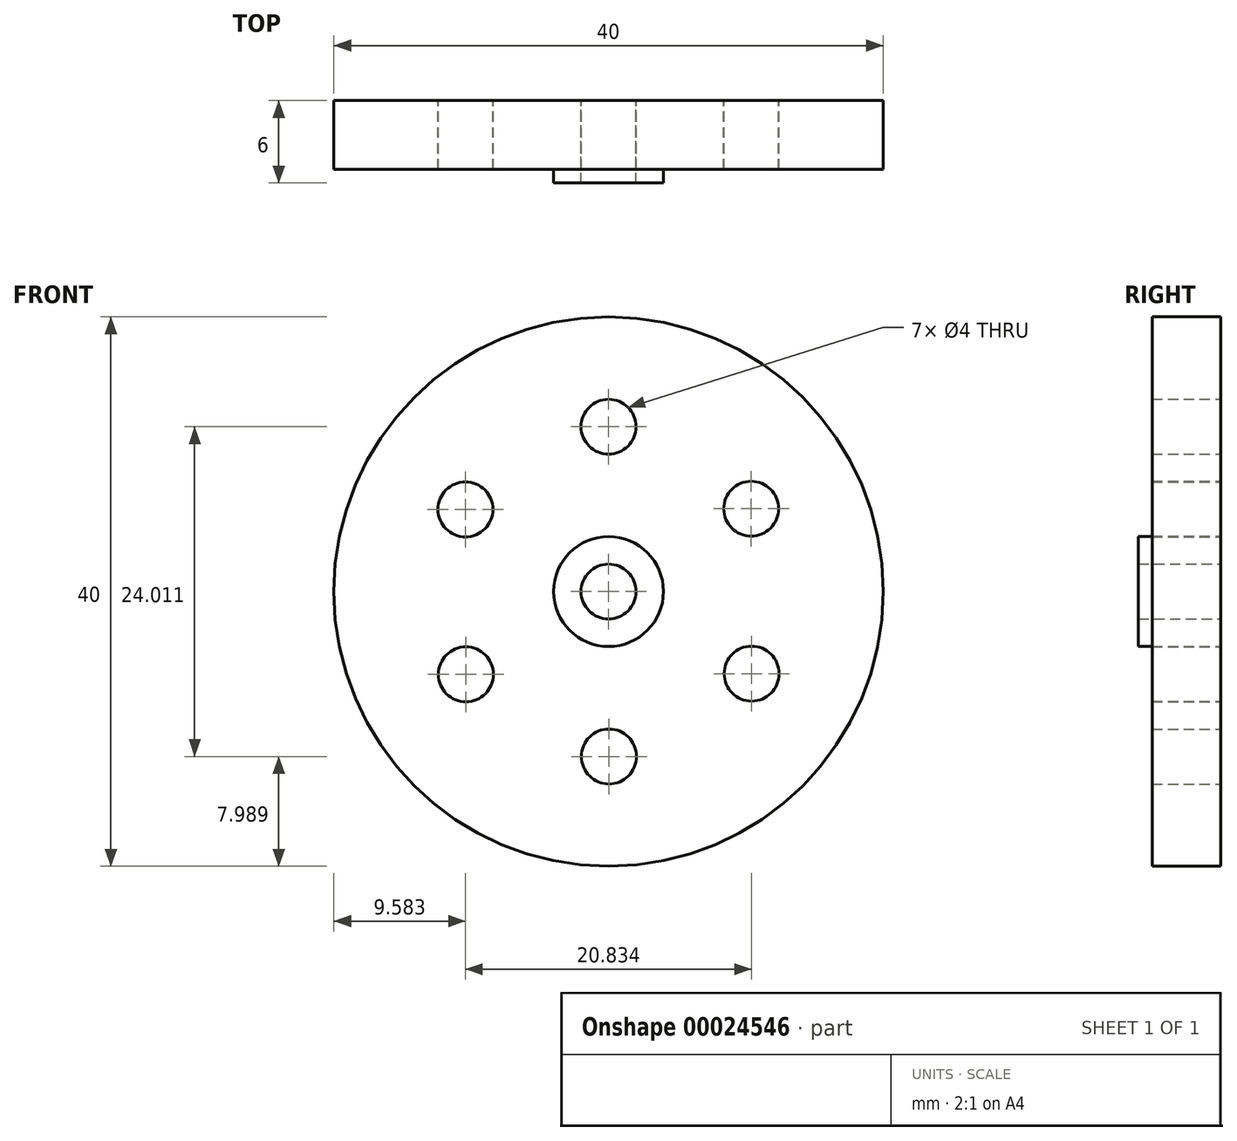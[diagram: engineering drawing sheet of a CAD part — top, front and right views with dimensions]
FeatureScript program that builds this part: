
annotation { "Feature Type Name" : "Feature", "Feature Type Description" : "" }
export const myFeature = defineFeature(function(context is Context, id is Id, definition is map)
    precondition{}
    {
        {
            var Q0;
            Q0=qCreatedBy(makeId("Front.planeOp"),FACE);
            var sketch = newSketch(context, id + "F0", { "sketchPlane" : qUnion([Q0])});
            skCircle(sketch, "E0", {"center": v(0, 0) * mm, "radius": 20 * mm});
            skCircle(sketch, "E1", {"center": v(0, 0) * mm, "radius": 4 * mm});
            skLineSegment(sketch, "E2", {"start": v(0, 0) * mm, "end": v(0, 12) * mm});
            skCircle(sketch, "E3.cCircle", {"center": v(0, 0) * mm, "radius": 10.4 * mm, "construction": true});
            skLineSegment(sketch, "E3.0", {"start": v(10.42, -5.98) * mm, "end": v(0.03, -12.01) * mm});
            skLineSegment(sketch, "E3.1", {"start": v(0.03, -12.01) * mm, "end": v(-10.39, -6.03) * mm});
            skLineSegment(sketch, "E3.2", {"start": v(-10.39, -6.03) * mm, "end": v(-10.42, 5.98) * mm});
            skLineSegment(sketch, "E3.3", {"start": v(-10.42, 5.98) * mm, "end": v(-0.03, 12.01) * mm});
            skLineSegment(sketch, "E3.4", {"start": v(-0.03, 12.01) * mm, "end": v(10.39, 6.03) * mm});
            skLineSegment(sketch, "E3.5", {"start": v(10.39, 6.03) * mm, "end": v(10.42, -5.98) * mm});
            skPoint(sketch, "E3.0.midPoint", {"position": v(5.22, -9) * mm});
            skCircle(sketch, "E4", {"center": v(-10.42, 5.98) * mm, "radius": 2 * mm});
            skCircle(sketch, "E5", {"center": v(0, 12) * mm, "radius": 2 * mm});
            skCircle(sketch, "E6", {"center": v(10.39, 6.03) * mm, "radius": 2 * mm});
            skCircle(sketch, "E7", {"center": v(10.42, -5.98) * mm, "radius": 2 * mm});
            skCircle(sketch, "E8", {"center": v(0.03, -12.01) * mm, "radius": 2 * mm});
            skCircle(sketch, "E9", {"center": v(-10.39, -6.03) * mm, "radius": 2 * mm});
            skCircle(sketch, "E10", {"center": v(0, 0) * mm, "radius": 2 * mm});
            skLineSegment(sketch, "E11", {"start": v(0, 0) * mm, "end": v(0, 20) * mm});
            skSolve(sketch);
        }
        {
            var Q0;
            Q0=makeQuery(id+"F0.imprint","IMPRINT",FACE,{"disambiguationData":[TD([[makeQuery(id+"F0.imprint","IMPRINT",EDGE,{"derivedFrom":sQuery(id+"F0.wireOp",EDGE,"E0")}),1.0]])]});
            var Q1;
            Q1=makeQuery(id+"F0.imprint","IMPRINT",FACE,{"disambiguationData":[TD([[makeQuery(id+"F0.imprint","IMPRINT",EDGE,{"derivedFrom":sQuery(id+"F0.wireOp",EDGE,"E1")}),-1.0]])]});
            extrude(context, id + "F1", {"entities" : qUnion([Q0, Q1]), "depth" : 5 * mm});
        }
        {
            var Q0;
            Q0=makeQuery(id+"F0.imprint","IMPRINT",FACE,{"disambiguationData":[TD([[makeQuery(id+"F0.imprint","IMPRINT",EDGE,{"derivedFrom":sQuery(id+"F0.wireOp",EDGE,"E1")}),1.0]])]});
            extrude(context, id + "F2", {"entities" : qUnion([Q0]), "operationType" : NewBodyOperationType.ADD, "depth" : 6 * mm});
        }
    });
